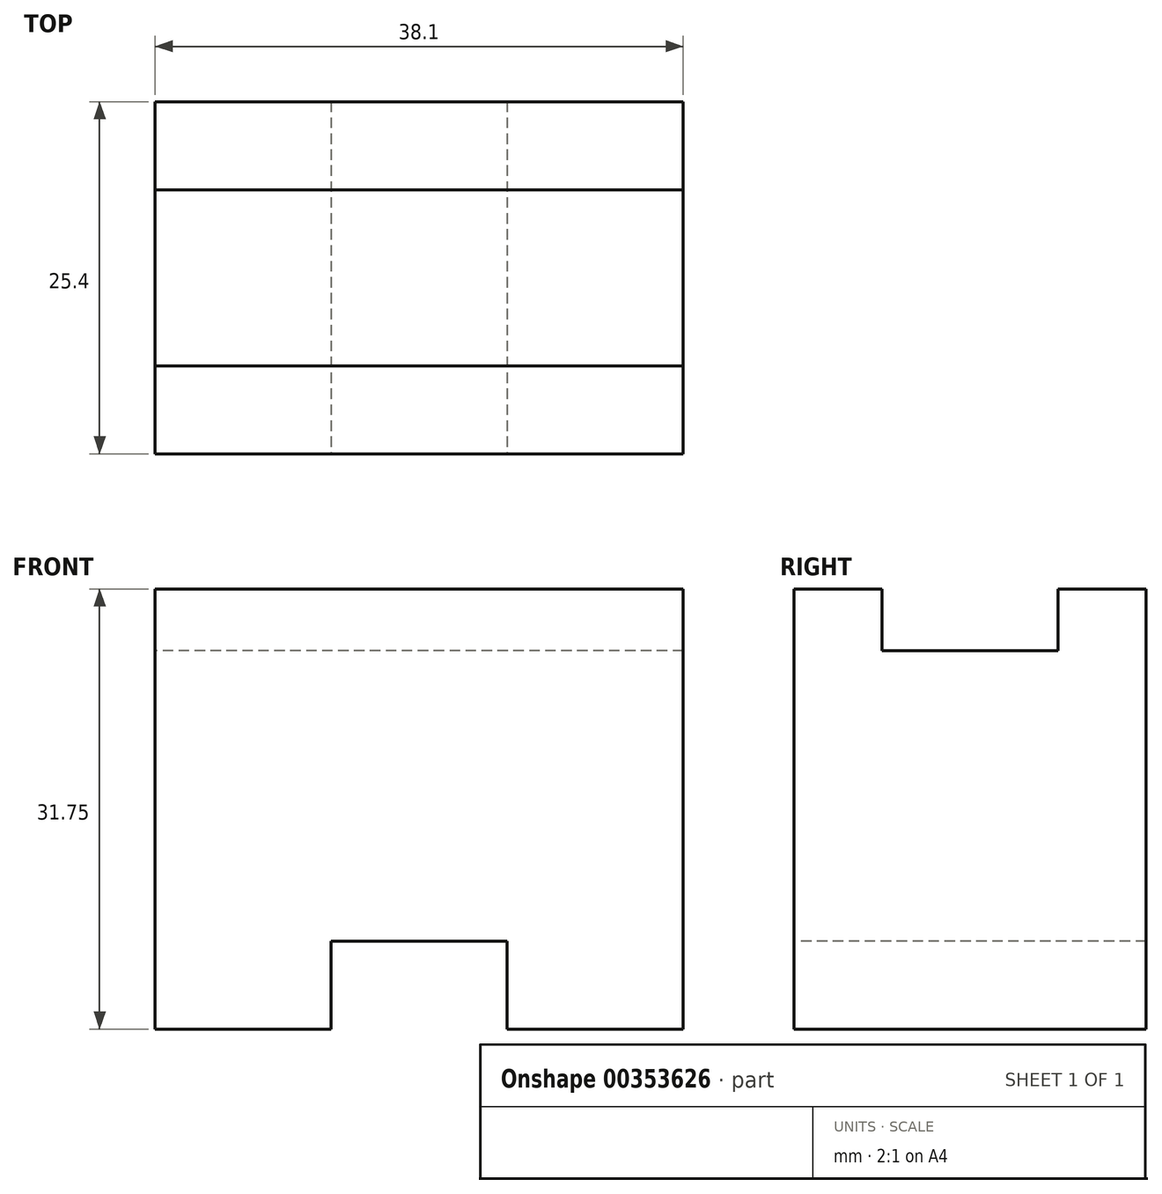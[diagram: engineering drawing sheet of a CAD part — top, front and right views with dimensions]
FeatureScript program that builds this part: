
annotation { "Feature Type Name" : "Feature", "Feature Type Description" : "" }
export const myFeature = defineFeature(function(context is Context, id is Id, definition is map)
    precondition{}
    {
        {
            var Q0;
            Q0=qCreatedBy(makeId("Right.planeOp"),FACE);
            var sketch = newSketch(context, id + "F0", { "sketchPlane" : qUnion([Q0])});
            skLineSegment(sketch, "E0", {"start": v(0, 31.75) * mm, "end": v(0, 0) * mm});
            skLineSegment(sketch, "E1", {"start": v(0, 0) * mm, "end": v(25.4, 0) * mm});
            skLineSegment(sketch, "E2", {"start": v(25.4, 0) * mm, "end": v(25.4, 31.75) * mm});
            skLineSegment(sketch, "E3", {"start": v(25.4, 31.75) * mm, "end": v(19.05, 31.75) * mm});
            skLineSegment(sketch, "E4", {"start": v(19.05, 31.75) * mm, "end": v(19.05, 27.3) * mm});
            skLineSegment(sketch, "E5", {"start": v(19.05, 27.3) * mm, "end": v(6.35, 27.3) * mm});
            skLineSegment(sketch, "E6", {"start": v(6.35, 27.3) * mm, "end": v(6.35, 31.75) * mm});
            skLineSegment(sketch, "E7", {"start": v(6.35, 31.75) * mm, "end": v(0, 31.75) * mm});
            skSolve(sketch);
        }
        {
            var Q0;
            Q0=makeQuery(id+"F0.imprint","IMPRINT",FACE,{"disambiguationData":[TD([[makeQuery(id+"F0.imprint","IMPRINT",EDGE,{"derivedFrom":sQuery(id+"F0.wireOp",EDGE,"E0")}),1.0]])]});
            extrude(context, id + "F1", {"entities" : qUnion([Q0]), "depth" : 38.1 * mm});
        }
        {
            var Q0;
            Q0=makeQuery(id+"F1.opExtrude","SWEPT_FACE",FACE,{"disambiguationData":[OSD([sQuery(id+"F0.wireOp",EDGE,"E0")])]});
            var sketch = newSketch(context, id + "F2", { "sketchPlane" : qUnion([Q0])});
            skLineSegment(sketch, "E8", {"start": v(12.7, 0) * mm, "end": v(12.7, 6.35) * mm});
            skLineSegment(sketch, "E9", {"start": v(12.7, 6.35) * mm, "end": v(25.4, 6.35) * mm});
            skLineSegment(sketch, "E10", {"start": v(25.4, 6.35) * mm, "end": v(25.4, 0) * mm});
            skSolve(sketch);
        }
        {
            var Q0;
            {var subQ0=sQuery(id+"F2.wireOp",EDGE,"E8");Q0=makeQuery(id+"F2.imprint","IMPRINT",FACE,{"disambiguationData":[TD([[makeQuery(id+"F2.imprint","IMPRINT",EDGE,{"derivedFrom":subQ0}),-1.0]])]});}
            extrude(context, id + "F3", {"entities" : qUnion([Q0]), "operationType" : NewBodyOperationType.REMOVE, "oppositeDirection" : true, "depth" : 25.4 * mm});
        }
    });
